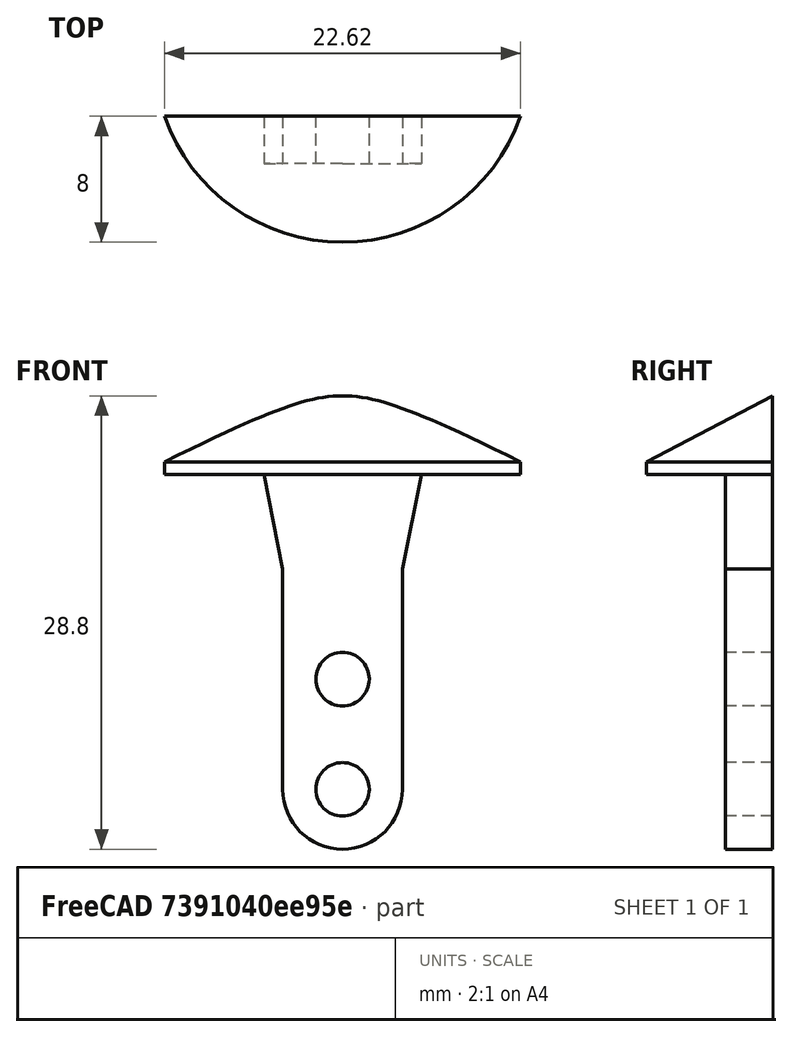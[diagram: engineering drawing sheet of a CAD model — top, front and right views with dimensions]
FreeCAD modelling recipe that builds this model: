
FCSTD DOCUMENT  (FreeCAD 0.19R24291 (Git))
Label: Зацеп
License: All rights reserved
LicenseURL: http://en.wikipedia.org/wiki/All_rights_reserved
objects: Sketcher::SketchObject×5, Mesh::Feature×1, PartDesign::Pad×1, PartDesign::Plane×1, PartDesign::Line×1, PartDesign::Revolution×1, PartDesign::Pocket×1, PartDesign::Mirrored×1, PartDesign::Body×1
note: 15 computed .brp shape members not serialized (recipe doc carries the construction recipe); baked Part::Feature solids carry a one-line shape summary decoded from their .brp

FEATURE [Mesh::Feature] Zacep4
FEATURE [Sketcher::SketchObject] Sketch
  FullyConstrained = true
  MapMode = 5
  Placement = pos=(0,0,0) rot=(1,0,0;1.5708rad)
  Support = -> [XZ_Plane]
  sketch-geometry (9):
    g0: ArcOfCircle CenterX=0 CenterY=3.8 CenterZ=0 NormalX=0 NormalY=0 NormalZ=1 AngleXU=0 Radius=1.7 StartAngle=4.71239 EndAngle=7.85398
    g1: ArcOfCircle CenterX=0 CenterY=3.8 CenterZ=0 NormalX=0 NormalY=0 NormalZ=1 AngleXU=0 Radius=3.8 StartAngle=4.71239 EndAngle=6.28319
    g2: ArcOfCircle CenterX=0 CenterY=10.8 CenterZ=0 NormalX=0 NormalY=0 NormalZ=1 AngleXU=0 Radius=1.7 StartAngle=4.71239 EndAngle=7.85398
    g3: LineSegment StartX=-3e-16 StartY=9.1 StartZ=0 EndX=5e-16 EndY=5.5 EndZ=0
    g4: LineSegment StartX=3.8 StartY=3.8 StartZ=0 EndX=3.8 EndY=17.8 EndZ=0
    g5: LineSegment StartX=5e-16 StartY=12.5 StartZ=0 EndX=5e-16 EndY=23.8 EndZ=0
    g6: LineSegment StartX=5e-16 StartY=23.8 StartZ=0 EndX=5 EndY=23.8 EndZ=0
    g7: LineSegment StartX=5 StartY=23.8 StartZ=0 EndX=3.8 EndY=17.8 EndZ=0
    g8: LineSegment StartX=-3e-16 StartY=2.1 StartZ=0 EndX=-7e-16 EndY=0 EndZ=0
  constraints (28):
    c: PointOnObject(g0,g-2)
    c: PointOnObject(g0,g-2)
    c: PointOnObject(g0,g-2)
    c: Coincident(g1,g0)
    c: Coincident(g1,g-1)
    c: Diameter(g1) = 7.6
    c: Diameter(g0) = 3.4
    c: PointOnObject(g2,g-2)
    c: PointOnObject(g2,g-2)
    c: Diameter(g2) = 3.4
    c: Distance(g0,g2) = 7
    c: Coincident(g3,g2)
    c: Coincident(g3,g0)
    c: Coincident(g4,g1)
    c: Vertical(g4)
    c: Coincident(g5,g2)
    c: PointOnObject(g5,g-2)
    c: Vertical(g5)
    c: Distance(g5) = 11.3
    c: Tangent(g4,g1)
    c: Coincident(g6,g5)
    c: Horizontal(g6)
    c: Coincident(g7,g6)
    c: Coincident(g7,g4)
    c: Distance(g6) = 5
    c: Distance(g4) = 14
    c: Coincident(g8,g0)
    c: Coincident(g8,g1)
FEATURE [PartDesign::Pad] Pad
  Direction = (1,1,1)
  Length = 3
  Length2 = 100
  Placement = pos=(0,0,0) rot=(1,0,0;1.5708rad)
  Profile = -> Sketch
  Type = 0
FEATURE [Sketcher::SketchObject] Sketch001
  FullyConstrained = false
  MapMode = 5
  Support = -> [XY_Plane]
  sketch-geometry (3):
    g0: ArcOfCircle CenterX=0 CenterY=4 CenterZ=0 NormalX=0 NormalY=0 NormalZ=1 AngleXU=0 Radius=12.5 StartAngle=4.71239 EndAngle=5.75414
    g1: ArcOfCircle CenterX=0 CenterY=4 CenterZ=0 NormalX=0 NormalY=0 NormalZ=1 AngleXU=0 Radius=4 StartAngle=4.71239 EndAngle=5.76104
    g2: LineSegment StartX=3.467 StartY=2.00502 StartZ=0 EndX=10.7911 EndY=-2.30884 EndZ=0
  constraints (8):
    c: PointOnObject(g0,g-2)
    c: PointOnObject(g0,g-2)
    c: Diameter(g0) = 25
    c: Coincident(g1,g0)
    c: Coincident(g1,g-1)
    c: Coincident(g2,g1)
    c: Coincident(g2,g0)
    c: Diameter(g1) = 8
FEATURE [PartDesign::Plane] DatumPlane
  Length = 60
  MapMode = 5
  Placement = pos=(0,1.59e-14,23.8) rot=(0,0,1;3.14159rad)
  ResizeMode = 0
  Support = -> [Pad]
  Width = 60
FEATURE [Sketcher::SketchObject] Sketch002
  FullyConstrained = true
  MapMode = 5
  Placement = pos=(0,1.59e-14,23.8) rot=(0,0,1;3.14159rad)
  Support = -> [DatumPlane]
FEATURE [Sketcher::SketchObject] Sketch003
  FullyConstrained = true
  MapMode = 5
  Placement = pos=(0,0,0) rot=(0.57735,0.57735,0.57735;2.0944rad)
  Support = -> [YZ_Plane]
  sketch-geometry (4):
    g0: LineSegment StartX=0 StartY=28.8 StartZ=0 EndX=-8 EndY=24.6 EndZ=0
    g1: LineSegment StartX=-8 StartY=24.6 StartZ=0 EndX=-8 EndY=23.8 EndZ=0
    g2: LineSegment StartX=-8 StartY=23.8 StartZ=0 EndX=0 EndY=23.8 EndZ=0
    g3: LineSegment StartX=0 StartY=23.8 StartZ=0 EndX=0 EndY=28.8 EndZ=0
  constraints (12):
    c: PointOnObject(g0,g-2)
    c: Coincident(g1,g0)
    c: Vertical(g1)
    c: Coincident(g2,g1)
    c: PointOnObject(g2,g-2)
    c: Horizontal(g2)
    c: Coincident(g3,g2)
    c: Coincident(g3,g0)
    c: Distance(g2,g-1) = 23.8
    c: Distance(g1) = 0.8
    c: Distance(g3) = 5
    c: Distance(g2) = 8
FEATURE [PartDesign::Line] DatumLine
  AttacherType = Attacher::AttachEngineLine
  Length = 20
  MapMode = 19
  Placement = pos=(0,4,0) rot=(0,0,1;4.71239rad)
  ResizeMode = 0
  Support = -> [Sketch001]
FEATURE [PartDesign::Revolution] Revolution
  Angle = 90
  Axis = (-1e-16,-1e-16,1)
  Base = (0,4,0)
  BaseFeature = -> Pad
  Placement = pos=(0,0,0) rot=(1,0,0;1.5708rad)
  Profile = -> Sketch003
  ReferenceAxis = -> DatumLine
FEATURE [Sketcher::SketchObject] Sketch004
  FullyConstrained = false
  MapMode = 5
  Support = -> [XY_Plane]
  sketch-geometry (4):
    g0: LineSegment StartX=0 StartY=0 StartZ=0 EndX=30.0652 EndY=0 EndZ=0
    g1: LineSegment StartX=30.0652 StartY=0 StartZ=0 EndX=30.0652 EndY=28.066 EndZ=0
    g2: LineSegment StartX=30.0652 StartY=28.066 StartZ=0 EndX=0 EndY=28.066 EndZ=0
    g3: LineSegment StartX=0 StartY=28.066 StartZ=0 EndX=0 EndY=0 EndZ=0
  constraints (9):
    c: Coincident(g0,g1)
    c: Coincident(g1,g2)
    c: Coincident(g2,g3)
    c: Coincident(g3,g0)
    c: Horizontal(g0)
    c: Horizontal(g2)
    c: Vertical(g1)
    c: Vertical(g3)
    c: Coincident(g0,g-1)
FEATURE [PartDesign::Pocket] Pocket
  BaseFeature = -> Revolution
  Length = 5
  Length2 = 100
  Midplane = true
  Placement = pos=(0,0,0) rot=(1,0,0;1.5708rad)
  Profile = -> Sketch004
  Type = 1
FEATURE [PartDesign::Mirrored] Mirrored
  BaseFeature = -> Pocket
  MirrorPlane = -> Sketch [V_Axis]
  Originals = -> [Pad,Revolution,Pocket]
  Placement = pos=(0,0,0) rot=(1,0,0;1.5708rad)
FEATURE [PartDesign::Body] Body
  Group = -> [Sketch,Pad,Sketch001,DatumPlane,Sketch002,Sketch003,DatumLine,Revolution,Sketch004,Pocket,Mirrored]
  Origin = -> Origin
  Tip = -> Mirrored
